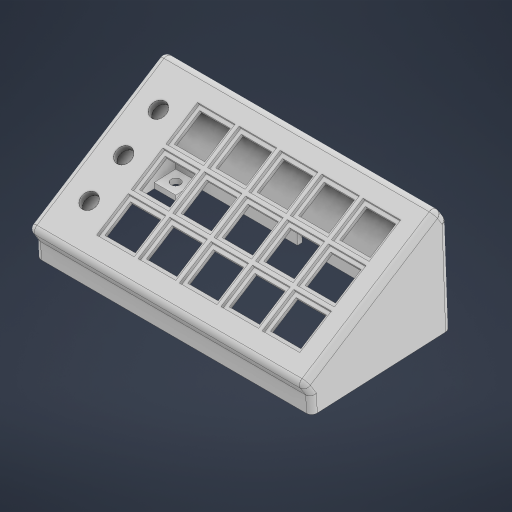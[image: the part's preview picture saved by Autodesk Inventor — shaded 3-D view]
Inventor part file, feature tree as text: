
AUTODESK INVENTOR PART (.ipt)
format: ipt  version: 2024.3 (Build 283343000, 343)  size: 863,232 bytes
history: native  units: mm
features: projected_geometry x65, sketch x14, extrude x10, fillet x2, other x2, plane x1, loft x1
ambient origin geometry x8: Origin, YZ Plane, XZ Plane, XY Plane, X Axis, Y Axis, Z Axis, Center Point
bodies: Solid1 (feature_tree)
feature tree (95):
  extrude  "Extrusion1"  Depth=126.85mm
  extrude  "Extrusion2"  Depth=17.3mm
  extrude  "Extrusion3"  Depth=9.65mm
  sketch  "Sketch6"  dims[d6=17.3mm d7=17.3mm d8=9.55mm d9=1.7mm]
  plane  "Work Plane2"
  extrude  "Extrusion5"  Depth=1.7mm
  sketch  "Sketch10"  dims[d14=17.3mm d15=17.3mm d16=17.3mm d17=17.3mm d18=1.7mm d19=17.3mm d20=17.3mm d21=1.7mm d22=1.7mm d23=28.6mm]
  extrude  "Extrusion6"  Depth=9.5mm
  extrude  "Extrusion8"  Depth=28.6mm
  sketch  "Sketch17"  dims[d48=66.65mm d49=66.65mm]
  extrude  "Extrusion9"  Depth=0.117617mm
  loft  "Loft4"
  sketch  "Sketch19"  dims[d60=85.65mm d61=85.65mm]
  fillet  "Fillet1"  Radius=9.65mm
  fillet  "Fillet2"  Radius=47.6mm
  extrude  "Extrusion10"  Depth=66.65mm
  extrude  "Extrusion11"  Depth=9.65mm
  extrude  "Extrusion12"  Depth=85.65mm
  sketch  "Sketch1"  dims[d0=74.6mm d1=126.85mm]
  sketch  "Sketch3"  dims[d2=17.3mm d3=17.3mm]
  projected_geometry  "Projected Loop2"
  projected_geometry  "Projected Loop3"
  projected_geometry  "Projected Loop4"
  projected_geometry  "Projected Loop5"
  projected_geometry  "Projected Loop6"
  projected_geometry  "Projected Loop7"
  projected_geometry  "Projected Loop8"
  projected_geometry  "Projected Loop9"
  projected_geometry  "Projected Loop10"
  projected_geometry  "Projected Loop11"
  projected_geometry  "Projected Loop12"
  projected_geometry  "Projected Loop13"
  projected_geometry  "Projected Loop14"
  projected_geometry  "Projected Loop15"
  projected_geometry  "Projected Loop16"
  projected_geometry  "Projected Loop17"
  projected_geometry  "Projected Loop18"
  projected_geometry  "Projected Loop19"
  projected_geometry  "Projected Loop20"
  projected_geometry  "Projected Loop21"
  projected_geometry  "Projected Loop22"
  projected_geometry  "Projected Loop23"
  projected_geometry  "Projected Loop24"
  projected_geometry  "Projected Loop25"
  projected_geometry  "Projected Loop26"
  projected_geometry  "Projected Loop27"
  projected_geometry  "Projected Loop28"
  projected_geometry  "Projected Loop29"
  projected_geometry  "Projected Loop30"
  projected_geometry  "Projected Loop31"
  projected_geometry  "Projected Loop32"
  projected_geometry  "Projected Loop33"
  projected_geometry  "Projected Loop34"
  projected_geometry  "Projected Loop35"
  projected_geometry  "Projected Loop36"
  projected_geometry  "Projected Loop37"
  projected_geometry  "Projected Loop38"
  projected_geometry  "Projected Loop39"
  projected_geometry  "Projected Loop40"
  projected_geometry  "Projected Loop41"
  projected_geometry  "Projected Loop42"
  projected_geometry  "Projected Loop43"
  projected_geometry  "Projected Loop44"
  projected_geometry  "Projected Loop45"
  projected_geometry  "Projected Loop46"
  projected_geometry  "Projected Loop47"
  projected_geometry  "Projected Loop48"
  projected_geometry  "Projected Loop49"
  projected_geometry  "Projected Loop50"
  projected_geometry  "Projected Loop51"
  projected_geometry  "Projected Loop52"
  projected_geometry  "Projected Loop53"
  projected_geometry  "Projected Loop54"
  projected_geometry  "Projected Loop55"
  projected_geometry  "Projected Loop56"
  projected_geometry  "Projected Loop57"
  projected_geometry  "Projected Loop58"
  projected_geometry  "Projected Loop59"
  projected_geometry  "Projected Loop60"
  projected_geometry  "Projected Loop61"
  projected_geometry  "Projected Loop62"
  sketch  "Sketch5"  dims[d4=9.55mm d5=9.65mm]
  projected_geometry  "Projected Loop63"
  projected_geometry  "Projected Loop64"
  sketch  "Sketch9"  dims[d10=17.3mm d11=17.3mm d12=1.7mm d13=9.5mm]
  projected_geometry  "Projected Loop66"
  sketch  "Sketch14"  dims[d24=28.6mm d25=0.117617mm]
  sketch  "Sketch16"  dims[d26=17.3mm d27=17.3mm d28=17.3mm d29=17.3mm d30=1.7mm d31=17.3mm d32=17.3mm d33=1.7mm d34=17.3mm d35=17.3mm d36=17.3mm d37=17.3mm d38=1.7mm d39=17.3mm d40=17.3mm d41=1.7mm d42=1.7mm d43=0.117617mm d44=1.7mm d45=1.7mm d46=9.65mm d47=47.6mm]
  sketch  "Sketch18"  dims[d50=17.3mm d51=17.3mm d52=17.3mm d53=17.3mm d54=1.7mm d55=17.3mm d56=17.3mm d57=1.7mm d58=1.7mm d59=9.65mm]
  other  "Edges7"
  other  "Edges8"
  sketch  "Sketch20"  dims[d62=7.2mm]
  sketch  "Sketch21"  dims[d63=10.7mm]
  projected_geometry  "Projected Loop70"
  sketch  "Sketch22"  dims[d64=8.65mm d65=7.2mm d66=10.7mm d67=8.65mm d68=7.2mm d69=8.65mm d70=10.7mm d71=3.0mm d72=0.0mm d133=1.5mm d134=0.0mm d141=2.5mm d142=2.5mm d143=2.5mm d144=2.5mm d145=4.3mm d146=0.0mm d148=120.0deg d152=7.5mm d153=0.0mm d166=2.5mm d167=0.0mm d170=2.5mm d171=0.0mm d172=2.5mm d173=0.0mm d174=0.0mm d175=90.0deg d176=0.0mm d177=90.0deg d178=2.5mm d179=2.5mm d180=10.0mm d181=10.0mm d182=10.0mm d183=10.0mm d184=10.0mm d185=10.0mm d186=10.0mm d187=10.0mm d188=2.5mm d189=0.0mm d190=4.3mm d191=5.0mm d192=5.0mm d193=4.3mm d194=5.0mm d195=5.0mm d196=4.3mm d197=5.0mm d198=5.0mm d199=4.3mm d200=5.0mm d201=5.0mm d202=2.5mm d203=0.0mm d204=0.0mm d205=6.0mm d206=10.0mm d207=55.925mm d208=2.5mm d209=0.0mm d135=0.5mm d136=0.872665mm]
